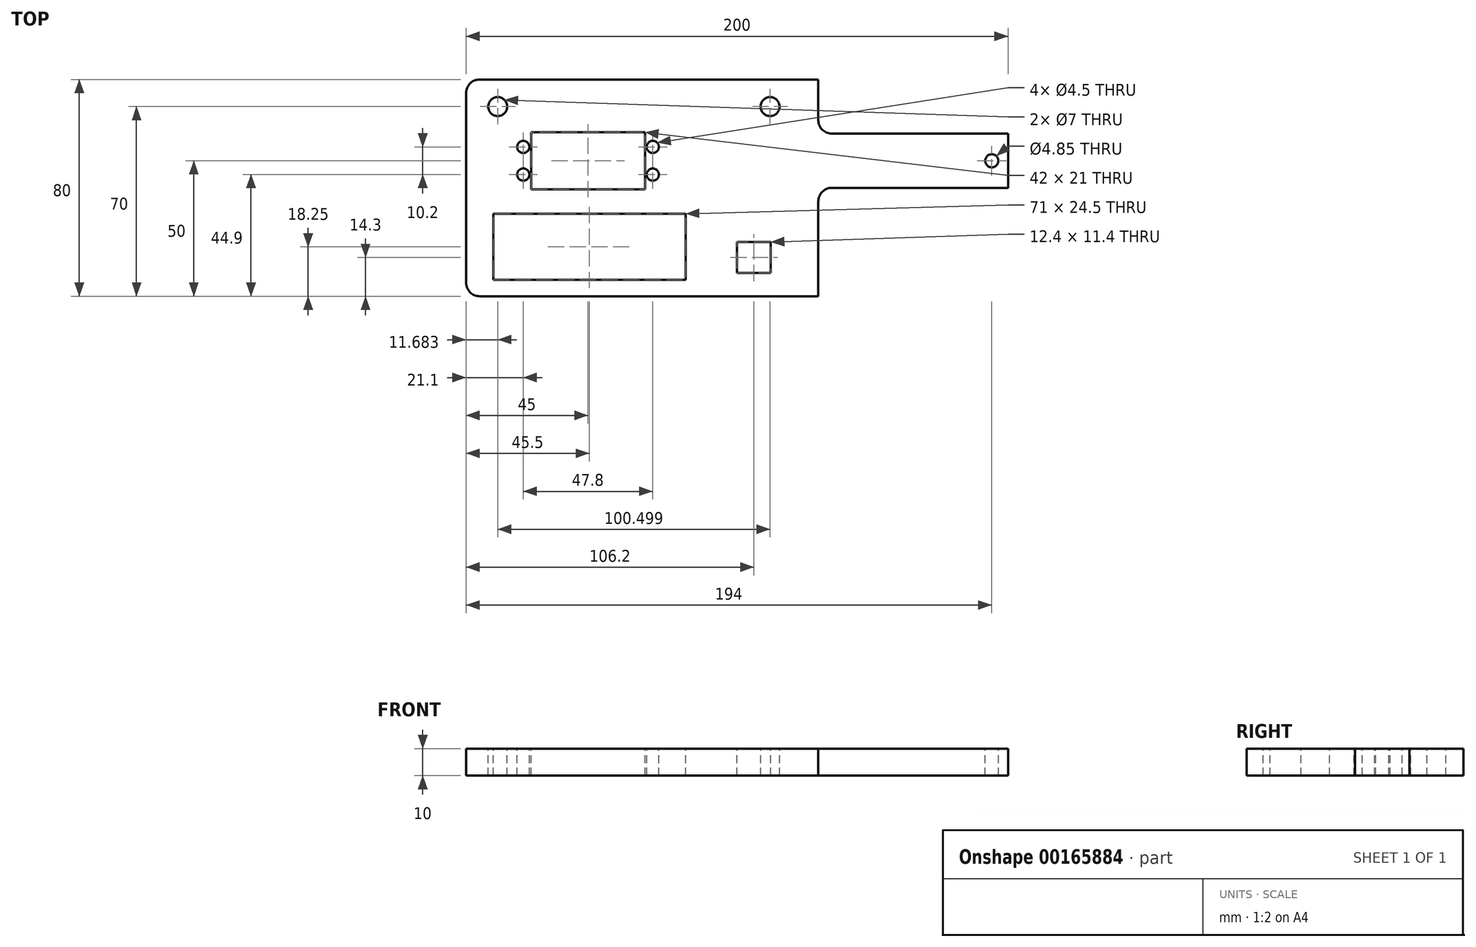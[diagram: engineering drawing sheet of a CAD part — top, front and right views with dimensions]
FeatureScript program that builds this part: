
annotation { "Feature Type Name" : "Feature", "Feature Type Description" : "" }
export const myFeature = defineFeature(function(context is Context, id is Id, definition is map)
    precondition{}
    {
        {
            var Q0;
            Q0=qCreatedBy(makeId("Top.planeOp"),FACE);
            var sketch = newSketch(context, id + "F0", { "sketchPlane" : qUnion([Q0])});
            skLineSegment(sketch, "E0.bottom", {"start": v(100, -40) * mm, "end": v(-100, -40) * mm});
            skLineSegment(sketch, "E0.top", {"start": v(100, 40) * mm, "end": v(-100, 40) * mm});
            skLineSegment(sketch, "E0.left", {"start": v(100, -40) * mm, "end": v(100, 40) * mm});
            skLineSegment(sketch, "E0.right", {"start": v(-100, -40) * mm, "end": v(-100, 40) * mm});
            skPoint(sketch, "E0.middle", {"position": v(0, 0) * mm});
            skSolve(sketch);
        }
        {
            var Q0;
            Q0=makeQuery(id+"F0.imprint","IMPRINT",FACE,{"disambiguationData":[TD([[makeQuery(id+"F0.imprint","IMPRINT",EDGE,{"derivedFrom":sQuery(id+"F0.wireOp",EDGE,"E0.bottom")}),-1.0]])]});
            extrude(context, id + "F1", {"entities" : qUnion([Q0]), "depth" : 10 * mm});
        }
        {
            var Q0;
            Q0=makeQuery(id+"F1.opExtrude","CAP_FACE",FACE,{"disambiguationData":[OSD([sQuery(id+"F0.wireOp",EDGE,"E0.bottom"),sQuery(id+"F0.wireOp",EDGE,"E0.top"),sQuery(id+"F0.wireOp",EDGE,"E0.left"),sQuery(id+"F0.wireOp",EDGE,"E0.right")])],"isStart":false});
            var sketch = newSketch(context, id + "F2", { "sketchPlane" : qUnion([Q0])});
            skLineSegment(sketch, "E1.bottom", {"start": v(-76, -0.5) * mm, "end": v(-34, -0.5) * mm});
            skLineSegment(sketch, "E1.top", {"start": v(-76, 20.5) * mm, "end": v(-34, 20.5) * mm});
            skLineSegment(sketch, "E1.left", {"start": v(-76, -0.5) * mm, "end": v(-76, 20.5) * mm});
            skLineSegment(sketch, "E1.right", {"start": v(-34, -0.5) * mm, "end": v(-34, 20.5) * mm});
            skPoint(sketch, "E1.middle", {"position": v(-55, 10) * mm});
            skSolve(sketch);
        }
        {
            var Q0;
            Q0=makeQuery(id+"F2.imprint","IMPRINT",FACE,{"disambiguationData":[TD([[makeQuery(id+"F2.imprint","IMPRINT",EDGE,{"derivedFrom":sQuery(id+"F2.wireOp",EDGE,"E1.bottom")}),1.0]])]});
            extrude(context, id + "F3", {"entities" : qUnion([Q0]), "operationType" : NewBodyOperationType.REMOVE, "endBound" : BoundingType.THROUGH_ALL, "oppositeDirection" : true, "depth" : 25 * mm});
        }
        {
            var Q0;
            Q0=makeQuery(id+"F1.opExtrude","CAP_FACE",FACE,{"disambiguationData":[OSD([sQuery(id+"F0.wireOp",EDGE,"E0.bottom"),sQuery(id+"F0.wireOp",EDGE,"E0.top"),sQuery(id+"F0.wireOp",EDGE,"E0.left"),sQuery(id+"F0.wireOp",EDGE,"E0.right")])],"isStart":false});
            var sketch = newSketch(context, id + "F4", { "sketchPlane" : qUnion([Q0])});
            skLineSegment(sketch, "E2.bottom", {"start": v(-78.9, 15.1) * mm, "end": v(-31.1, 15.1) * mm});
            skLineSegment(sketch, "E2.top", {"start": v(-78.9, 4.9) * mm, "end": v(-31.1, 4.9) * mm});
            skLineSegment(sketch, "E2.left", {"start": v(-78.9, 15.1) * mm, "end": v(-78.9, 4.9) * mm});
            skLineSegment(sketch, "E2.right", {"start": v(-31.1, 15.1) * mm, "end": v(-31.1, 4.9) * mm});
            skPoint(sketch, "E2.middle", {"position": v(-55, 10) * mm});
            skPoint(sketch, "E2.middle.positionSnap0", {"position": v(-76, 10) * mm});
            skPoint(sketch, "E2.middle.positionSnap1", {"position": v(-55, -0.5) * mm});
            skPoint(sketch, "E2.centerSnap0", {"position": v(-76, 10) * mm});
            skPoint(sketch, "E2.centerSnap1", {"position": v(-55, -0.5) * mm});
            skCircle(sketch, "E3", {"center": v(-78.9, 15.1) * mm, "radius": 2.25 * mm});
            skCircle(sketch, "E4", {"center": v(-78.9, 4.9) * mm, "radius": 2.25 * mm});
            skCircle(sketch, "E5", {"center": v(-31.1, 15.1) * mm, "radius": 2.25 * mm});
            skCircle(sketch, "E6", {"center": v(-31.1, 4.9) * mm, "radius": 2.25 * mm});
            skLineSegment(sketch, "E7.bottom", {"start": v(-90, -9.5) * mm, "end": v(-19, -9.5) * mm});
            skLineSegment(sketch, "E7.top", {"start": v(-90, -34) * mm, "end": v(-19, -34) * mm});
            skLineSegment(sketch, "E7.left", {"start": v(-90, -9.5) * mm, "end": v(-90, -34) * mm});
            skLineSegment(sketch, "E7.right", {"start": v(-19, -9.5) * mm, "end": v(-19, -34) * mm});
            skSolve(sketch);
        }
        {
            var Q0;
            {var subQ0=sQuery(id+"F4.wireOp",EDGE,"E2.left");var subQ1=sQuery(id+"F4.wireOp",EDGE,"E2.bottom");var subQ2=makeQuery(id+"F4.imprint","INTERSECT",VERTEX,{"derivedFrom":[subQ1,subQ0]});Q0=makeQuery(id+"F4.imprint","IMPRINT",FACE,{"disambiguationData":[TD([[makeQuery(id+"F4.imprint","IMPRINT",EDGE,{"disambiguationData":[TD([[subQ2,-1.0]])],"derivedFrom":subQ1}),1.0]])]});}
            var Q1;
            {var subQ0=sQuery(id+"F4.wireOp",EDGE,"E2.left");var subQ1=sQuery(id+"F4.wireOp",EDGE,"E2.bottom");var subQ2=makeQuery(id+"F4.imprint","INTERSECT",VERTEX,{"derivedFrom":[subQ1,subQ0]});Q1=makeQuery(id+"F4.imprint","IMPRINT",FACE,{"disambiguationData":[TD([[makeQuery(id+"F4.imprint","IMPRINT",EDGE,{"disambiguationData":[TD([[subQ2,-1.0]])],"derivedFrom":subQ1}),-1.0]])]});}
            var Q2;
            {var subQ0=sQuery(id+"F4.wireOp",EDGE,"E2.left");var subQ1=sQuery(id+"F4.wireOp",EDGE,"E2.top");var subQ2=makeQuery(id+"F4.imprint","INTERSECT",VERTEX,{"derivedFrom":[subQ1,subQ0]});Q2=makeQuery(id+"F4.imprint","IMPRINT",FACE,{"disambiguationData":[TD([[makeQuery(id+"F4.imprint","IMPRINT",EDGE,{"disambiguationData":[TD([[subQ2,-1.0]])],"derivedFrom":subQ1}),-1.0]])]});}
            var Q3;
            {var subQ0=sQuery(id+"F4.wireOp",EDGE,"E2.left");var subQ1=sQuery(id+"F4.wireOp",EDGE,"E2.top");var subQ2=makeQuery(id+"F4.imprint","INTERSECT",VERTEX,{"derivedFrom":[subQ1,subQ0]});Q3=makeQuery(id+"F4.imprint","IMPRINT",FACE,{"disambiguationData":[TD([[makeQuery(id+"F4.imprint","IMPRINT",EDGE,{"disambiguationData":[TD([[subQ2,-1.0]])],"derivedFrom":subQ1}),1.0]])]});}
            var Q4;
            {var subQ0=sQuery(id+"F4.wireOp",EDGE,"E2.right");var subQ1=sQuery(id+"F4.wireOp",EDGE,"E2.bottom");var subQ2=makeQuery(id+"F4.imprint","INTERSECT",VERTEX,{"derivedFrom":[subQ1,subQ0]});Q4=makeQuery(id+"F4.imprint","IMPRINT",FACE,{"disambiguationData":[TD([[makeQuery(id+"F4.imprint","IMPRINT",EDGE,{"disambiguationData":[TD([[subQ2,1.0]])],"derivedFrom":subQ1}),-1.0]])]});}
            var Q5;
            {var subQ0=sQuery(id+"F4.wireOp",EDGE,"E2.right");var subQ1=sQuery(id+"F4.wireOp",EDGE,"E2.bottom");var subQ2=makeQuery(id+"F4.imprint","INTERSECT",VERTEX,{"derivedFrom":[subQ1,subQ0]});Q5=makeQuery(id+"F4.imprint","IMPRINT",FACE,{"disambiguationData":[TD([[makeQuery(id+"F4.imprint","IMPRINT",EDGE,{"disambiguationData":[TD([[subQ2,1.0]])],"derivedFrom":subQ1}),1.0]])]});}
            var Q6;
            {var subQ0=sQuery(id+"F4.wireOp",EDGE,"E2.right");var subQ1=sQuery(id+"F4.wireOp",EDGE,"E2.top");var subQ2=makeQuery(id+"F4.imprint","INTERSECT",VERTEX,{"derivedFrom":[subQ1,subQ0]});Q6=makeQuery(id+"F4.imprint","IMPRINT",FACE,{"disambiguationData":[TD([[makeQuery(id+"F4.imprint","IMPRINT",EDGE,{"disambiguationData":[TD([[subQ2,1.0]])],"derivedFrom":subQ1}),1.0]])]});}
            var Q7;
            {var subQ0=sQuery(id+"F4.wireOp",EDGE,"E2.right");var subQ1=sQuery(id+"F4.wireOp",EDGE,"E2.top");var subQ2=makeQuery(id+"F4.imprint","INTERSECT",VERTEX,{"derivedFrom":[subQ1,subQ0]});Q7=makeQuery(id+"F4.imprint","IMPRINT",FACE,{"disambiguationData":[TD([[makeQuery(id+"F4.imprint","IMPRINT",EDGE,{"disambiguationData":[TD([[subQ2,1.0]])],"derivedFrom":subQ1}),-1.0]])]});}
            var Q8;
            Q8=makeQuery(id+"F4.imprint","IMPRINT",FACE,{"disambiguationData":[TD([[makeQuery(id+"F4.imprint","IMPRINT",EDGE,{"derivedFrom":sQuery(id+"F4.wireOp",EDGE,"E7.bottom")}),-1.0]])]});
            extrude(context, id + "F5", {"entities" : qUnion([Q0, Q1, Q2, Q3, Q4, Q5, Q6, Q7, Q8]), "operationType" : NewBodyOperationType.REMOVE, "endBound" : BoundingType.THROUGH_ALL, "oppositeDirection" : true, "depth" : 25 * mm});
        }
        {
            var Q0;
            Q0=makeQuery(id+"F1.opExtrude","CAP_FACE",FACE,{"disambiguationData":[OSD([sQuery(id+"F0.wireOp",EDGE,"E0.bottom"),sQuery(id+"F0.wireOp",EDGE,"E0.top"),sQuery(id+"F0.wireOp",EDGE,"E0.left"),sQuery(id+"F0.wireOp",EDGE,"E0.right")])],"isStart":false});
            var sketch = newSketch(context, id + "F6", { "sketchPlane" : qUnion([Q0])});
            skCircle(sketch, "E8", {"center": v(-88.32, 30) * mm, "radius": 3.5 * mm});
            skCircle(sketch, "E9", {"center": v(12.18, 30) * mm, "radius": 3.5 * mm});
            skSolve(sketch);
        }
        {
            var Q0;
            Q0=makeQuery(id+"F6.imprint","IMPRINT",FACE,{"disambiguationData":[TD([[makeQuery(id+"F6.imprint","IMPRINT",EDGE,{"derivedFrom":sQuery(id+"F6.wireOp",EDGE,"E8")}),1.0]])]});
            var Q1;
            Q1=makeQuery(id+"F6.imprint","IMPRINT",FACE,{"disambiguationData":[TD([[makeQuery(id+"F6.imprint","IMPRINT",EDGE,{"derivedFrom":sQuery(id+"F6.wireOp",EDGE,"E9")}),1.0]])]});
            extrude(context, id + "F7", {"entities" : qUnion([Q0, Q1]), "operationType" : NewBodyOperationType.REMOVE, "endBound" : BoundingType.THROUGH_ALL, "oppositeDirection" : true, "depth" : 25 * mm});
        }
        {
            var Q0;
            Q0=makeQuery(id+"F1.opExtrude","SWEPT_EDGE",EDGE,{"disambiguationData":[OSD([sQuery(id+"F0.wireOp",EDGE,"E0.top"),sQuery(id+"F0.wireOp",EDGE,"E0.right")])]});
            var Q1;
            Q1=makeQuery(id+"F1.opExtrude","SWEPT_EDGE",EDGE,{"disambiguationData":[OSD([sQuery(id+"F0.wireOp",EDGE,"E0.bottom"),sQuery(id+"F0.wireOp",EDGE,"E0.right")])]});
            var Q2;
            Q2=makeQuery(id+"F1.opExtrude","SWEPT_EDGE",EDGE,{"disambiguationData":[OSD([sQuery(id+"F0.wireOp",EDGE,"E0.top"),sQuery(id+"F0.wireOp",EDGE,"E0.left")])]});
            var Q3;
            Q3=makeQuery(id+"F1.opExtrude","SWEPT_EDGE",EDGE,{"disambiguationData":[OSD([sQuery(id+"F0.wireOp",EDGE,"E0.bottom"),sQuery(id+"F0.wireOp",EDGE,"E0.left")])]});
            fillet(context, id + "F8", {"entities" : qUnion([Q0, Q1, Q2, Q3]), "radius" : 5 * mm, "tangentPropagation" : true, "allowEdgeOverflow" : false});
        }
        {
            var Q0;
            Q0=makeQuery(id+"F1.opExtrude","CAP_FACE",FACE,{"disambiguationData":[OSD([sQuery(id+"F0.wireOp",EDGE,"E0.bottom"),sQuery(id+"F0.wireOp",EDGE,"E0.top"),sQuery(id+"F0.wireOp",EDGE,"E0.left"),sQuery(id+"F0.wireOp",EDGE,"E0.right")])],"isStart":false});
            var sketch = newSketch(context, id + "F9", { "sketchPlane" : qUnion([Q0])});
            skLineSegment(sketch, "E10.bottom", {"start": v(0, -20) * mm, "end": v(12.4, -20) * mm});
            skLineSegment(sketch, "E10.top", {"start": v(0, -31.4) * mm, "end": v(12.4, -31.4) * mm});
            skLineSegment(sketch, "E10.left", {"start": v(0, -20) * mm, "end": v(0, -31.4) * mm});
            skLineSegment(sketch, "E10.right", {"start": v(12.4, -20) * mm, "end": v(12.4, -31.4) * mm});
            skSolve(sketch);
        }
        {
            var Q0;
            Q0=makeQuery(id+"F1.opExtrude","CAP_FACE",FACE,{"disambiguationData":[OSD([sQuery(id+"F0.wireOp",EDGE,"E0.bottom"),sQuery(id+"F0.wireOp",EDGE,"E0.top"),sQuery(id+"F0.wireOp",EDGE,"E0.left"),sQuery(id+"F0.wireOp",EDGE,"E0.right")])],"isStart":false});
            var sketch = newSketch(context, id + "F10", { "sketchPlane" : qUnion([Q0])});
            skLineSegment(sketch, "E11.bottom", {"start": v(-76, 10) * mm, "end": v(94, 10) * mm});
            skLineSegment(sketch, "E11.top", {"start": v(-76, -40) * mm, "end": v(94, -40) * mm});
            skLineSegment(sketch, "E11.left", {"start": v(-76, 10) * mm, "end": v(-76, -40) * mm});
            skLineSegment(sketch, "E11.right", {"start": v(94, 10) * mm, "end": v(94, -40) * mm});
            skCircle(sketch, "E12", {"center": v(94, 10) * mm, "radius": 2.43 * mm});
            skSolve(sketch);
        }
        {
            var Q0;
            {var subQ0=sQuery(id+"F10.wireOp",EDGE,"E11.right");Q0=makeQuery(id+"F10.imprint","IMPRINT",FACE,{"disambiguationData":[TD([[makeQuery(id+"F10.imprint","IMPRINT",EDGE,{"derivedFrom":subQ0}),1.0]])]});}
            var sketch = newSketch(context, id + "F11", { "sketchPlane" : qUnion([Q0])});
            skLineSegment(sketch, "E13.bottom", {"start": v(100, 20) * mm, "end": v(30, 20) * mm});
            skLineSegment(sketch, "E13.top", {"start": v(100, 40) * mm, "end": v(30, 40) * mm});
            skLineSegment(sketch, "E13.left", {"start": v(100, 20) * mm, "end": v(100, 40) * mm});
            skLineSegment(sketch, "E13.right", {"start": v(30, 20) * mm, "end": v(30, 40) * mm});
            skLineSegment(sketch, "E14.bottom", {"start": v(30, 0) * mm, "end": v(100, 0) * mm});
            skLineSegment(sketch, "E14.top", {"start": v(30, -40) * mm, "end": v(100, -40) * mm});
            skLineSegment(sketch, "E14.left", {"start": v(30, 0) * mm, "end": v(30, -40) * mm});
            skLineSegment(sketch, "E14.right", {"start": v(100, 0) * mm, "end": v(100, -40) * mm});
            skSolve(sketch);
        }
        {
            var Q0;
            Q0=qSketchRegion(id+"F11",true);
            var Q1;
            {var subQ0=sQuery(id+"F10.wireOp",EDGE,"E11.right");var subQ1=sQuery(id+"F10.wireOp",EDGE,"E11.bottom");var subQ2=makeQuery(id+"F10.imprint","INTERSECT",VERTEX,{"derivedFrom":[subQ1,subQ0]});Q1=makeQuery(id+"F10.imprint","IMPRINT",FACE,{"disambiguationData":[TD([[makeQuery(id+"F10.imprint","IMPRINT",EDGE,{"disambiguationData":[TD([[subQ2,1.0]])],"derivedFrom":subQ1}),1.0]])]});}
            var Q2;
            {var subQ0=sQuery(id+"F10.wireOp",EDGE,"E11.right");var subQ1=sQuery(id+"F10.wireOp",EDGE,"E11.bottom");var subQ2=makeQuery(id+"F10.imprint","INTERSECT",VERTEX,{"derivedFrom":[subQ1,subQ0]});Q2=makeQuery(id+"F10.imprint","IMPRINT",FACE,{"disambiguationData":[TD([[makeQuery(id+"F10.imprint","IMPRINT",EDGE,{"disambiguationData":[TD([[subQ2,1.0]])],"derivedFrom":subQ1}),-1.0]])]});}
            var Q3;
            Q3=makeQuery(id+"F9.imprint","IMPRINT",FACE,{"disambiguationData":[TD([[makeQuery(id+"F9.imprint","IMPRINT",EDGE,{"derivedFrom":sQuery(id+"F9.wireOp",EDGE,"E10.bottom")}),-1.0]])]});
            extrude(context, id + "F12", {"entities" : qUnion([Q0, Q1, Q2, Q3]), "operationType" : NewBodyOperationType.REMOVE, "endBound" : BoundingType.THROUGH_ALL, "oppositeDirection" : true, "depth" : 25 * mm});
        }
        {
            var Q0;
            Q0=makeQuery(id+"F12.boolean.opBoolean","COPY",EDGE,{"derivedFrom":makeQuery(id+"F12.opExtrude","SWEPT_EDGE",EDGE,{"disambiguationData":[OSD([sQuery(id+"F0.wireOp",EDGE,"E0.top"),sQuery(id+"F11.wireOp",EDGE,"E13.top"),sQuery(id+"F11.wireOp",EDGE,"E13.right")])]})});
            var Q1;
            Q1=makeQuery(id+"F12.boolean.opBoolean","COPY",EDGE,{"derivedFrom":makeQuery(id+"F12.opExtrude","SWEPT_EDGE",EDGE,{"disambiguationData":[OSD([sQuery(id+"F11.wireOp",EDGE,"E13.bottom"),sQuery(id+"F11.wireOp",EDGE,"E13.right")])]})});
            var Q2;
            Q2=makeQuery(id+"F12.boolean.opBoolean","COPY",EDGE,{"derivedFrom":makeQuery(id+"F12.opExtrude","SWEPT_EDGE",EDGE,{"disambiguationData":[OSD([sQuery(id+"F0.wireOp",EDGE,"E0.left"),sQuery(id+"F11.wireOp",EDGE,"E13.bottom"),sQuery(id+"F11.wireOp",EDGE,"E13.left")])]})});
            var Q3;
            Q3=makeQuery(id+"F12.boolean.opBoolean","COPY",EDGE,{"derivedFrom":makeQuery(id+"F12.opExtrude","SWEPT_EDGE",EDGE,{"disambiguationData":[OSD([sQuery(id+"F11.wireOp",EDGE,"E14.top"),sQuery(id+"F11.wireOp",EDGE,"E14.left")])]})});
            var Q4;
            Q4=makeQuery(id+"F12.boolean.opBoolean","COPY",EDGE,{"derivedFrom":makeQuery(id+"F12.opExtrude","SWEPT_EDGE",EDGE,{"disambiguationData":[OSD([sQuery(id+"F11.wireOp",EDGE,"E14.bottom"),sQuery(id+"F11.wireOp",EDGE,"E14.right")])]})});
            var Q5;
            Q5=makeQuery(id+"F12.boolean.opBoolean","COPY",EDGE,{"derivedFrom":makeQuery(id+"F12.opExtrude","SWEPT_EDGE",EDGE,{"disambiguationData":[OSD([sQuery(id+"F11.wireOp",EDGE,"E14.bottom"),sQuery(id+"F11.wireOp",EDGE,"E14.left")])]})});
            fillet(context, id + "F13", {"entities" : qUnion([Q0, Q1, Q2, Q3, Q4, Q5]), "radius" : 5 * mm, "tangentPropagation" : true, "allowEdgeOverflow" : false});
        }
    });
